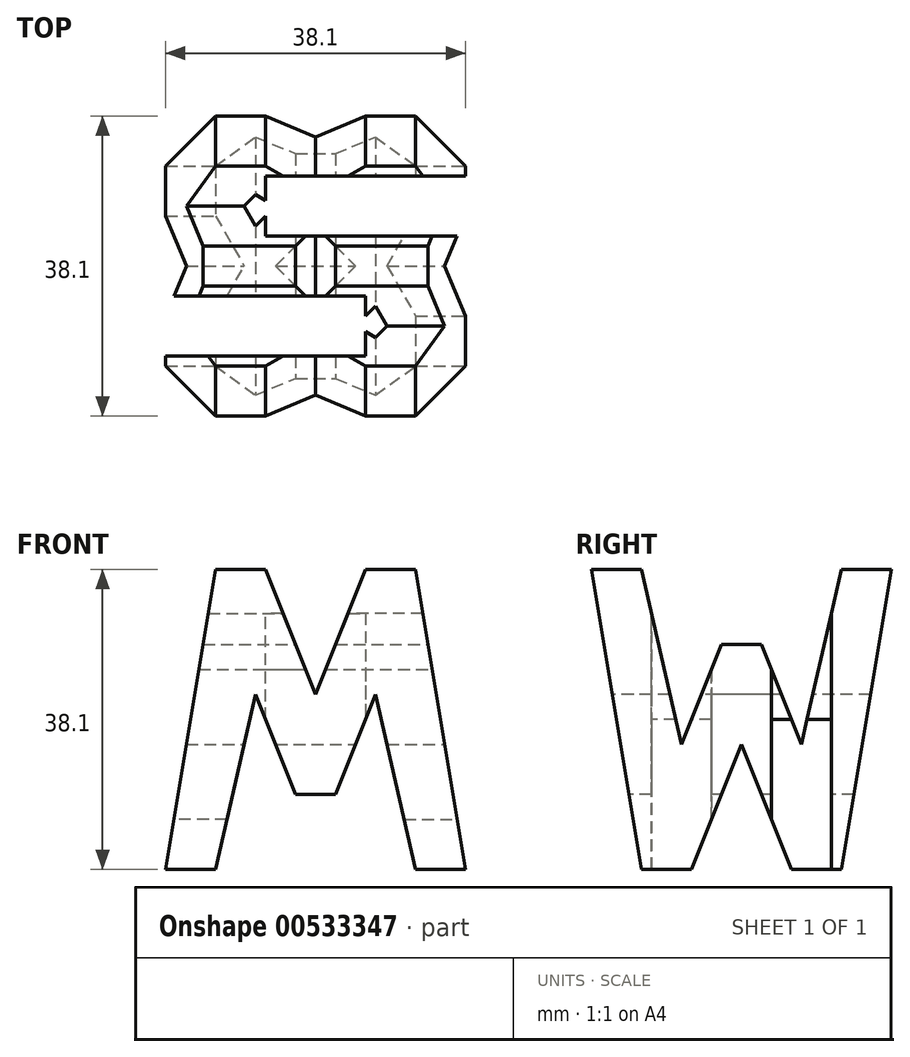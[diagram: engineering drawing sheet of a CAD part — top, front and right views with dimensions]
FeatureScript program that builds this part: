
annotation { "Feature Type Name" : "Feature", "Feature Type Description" : "" }
export const myFeature = defineFeature(function(context is Context, id is Id, definition is map)
    precondition{}
    {
        {
            var Q0;
            Q0=qCreatedBy(makeId("Front.planeOp"),FACE);
            var sketch = newSketch(context, id + "F0", { "sketchPlane" : qUnion([Q0])});
            skLineSegment(sketch, "E0", {"start": v(0, 0) * mm, "end": v(0, 38.1) * mm});
            skLineSegment(sketch, "E1", {"start": v(0, 38.1) * mm, "end": v(38.1, 38.1) * mm});
            skLineSegment(sketch, "E2", {"start": v(38.1, 38.1) * mm, "end": v(38.1, 0) * mm});
            skLineSegment(sketch, "E3", {"start": v(38.1, 0) * mm, "end": v(0, 0) * mm});
            skSolve(sketch);
        }
        {
            var Q0;
            Q0 = qSketchRegion(id + "F0", true);
            extrude(context, id + "F1", {"entities" : qUnion([Q0]), "depth" : 38.1 * mm, "offsetDistance" : 25.4 * mm});
        }
        {
            var Q0;
            Q0=qCreatedBy(makeId("Front.planeOp"),FACE);
            cPlane(context, id + "F2", {"entities" : qUnion([Q0]), "cplaneType" : CPlaneType.OFFSET, "offset" : 38.1 * mm, "width" : 152.4 * mm, "height" : 152.4 * mm});
        }
        {
            var Q0;
            Q0=qCreatedBy(makeId("Right.planeOp"),FACE);
            cPlane(context, id + "F3", {"entities" : qUnion([Q0]), "cplaneType" : CPlaneType.OFFSET, "offset" : 38.1 * mm, "width" : 152.4 * mm, "height" : 152.4 * mm});
        }
        {
            var Q0;
            Q0=qCreatedBy(makeId("Top.planeOp"),FACE);
            cPlane(context, id + "F4", {"entities" : qUnion([Q0]), "cplaneType" : CPlaneType.OFFSET, "offset" : 38.1 * mm, "width" : 152.4 * mm, "height" : 152.4 * mm});
        }
        {
            var Q0;
            Q0=qCreatedBy(id+"F3.planeOp",FACE);
            var sketch = newSketch(context, id + "F5", { "sketchPlane" : qUnion([Q0])});
            skLineSegment(sketch, "E4", {"start": v(-38.1, 38.1) * mm, "end": v(0, 38.1) * mm});
            skLineSegment(sketch, "E5", {"start": v(0, 38.1) * mm, "end": v(0, 0) * mm});
            skLineSegment(sketch, "E6", {"start": v(0, 0) * mm, "end": v(-38.1, 0) * mm});
            skLineSegment(sketch, "E7", {"start": v(-38.1, 0) * mm, "end": v(-38.1, 38.1) * mm});
            skLineSegment(sketch, "E8", {"start": v(-38.1, 38.1) * mm, "end": v(-31.75, 0) * mm});
            skLineSegment(sketch, "E9", {"start": v(0, 38.1) * mm, "end": v(-6.35, 0) * mm});
            skPoint(sketch, "E10.start.orphan", {"position": v(-28.95, 16.47) * mm});
            skPoint(sketch, "E11.end.orphan", {"position": v(-13.57, 16.47) * mm});
            skLineSegment(sketch, "E12", {"start": v(-6.35, 38.1) * mm, "end": v(-11.43, 15.87) * mm});
            skLineSegment(sketch, "E13", {"start": v(-26.67, 15.87) * mm, "end": v(-31.75, 38.1) * mm});
            skLineSegment(sketch, "E14", {"start": v(-19.05, 15.87) * mm, "end": v(-12.7, 0) * mm});
            skLineSegment(sketch, "E15", {"start": v(-19.05, 15.87) * mm, "end": v(-25.4, 0) * mm});
            skLineSegment(sketch, "E16", {"start": v(-26.67, 15.87) * mm, "end": v(-21.59, 28.57) * mm});
            skPoint(sketch, "E17.start.orphan", {"position": v(-21.6, 21.09) * mm});
            skPoint(sketch, "E18.end.orphan", {"position": v(-16.9, 28.57) * mm});
            skLineSegment(sketch, "E19", {"start": v(-21.6, 28.57) * mm, "end": v(-16.51, 28.57) * mm});
            skLineSegment(sketch, "E20", {"start": v(-16.51, 28.57) * mm, "end": v(-11.43, 15.87) * mm});
            skSolve(sketch);
        }
        {
            var Q0;
            {var subQ1=sQuery(id+"F5.wireOp",EDGE,"E12");Q0=makeQuery(id+"F5.imprint","IMPRINT",FACE,{"disambiguationData":[TD([[makeQuery(id+"F5.imprint","IMPRINT",EDGE,{"derivedFrom":subQ1}),-1.0]])]});}
            var Q1;
            {var subQ0=sQuery(id+"F5.wireOp",EDGE,"E7");Q1=makeQuery(id+"F5.imprint","IMPRINT",FACE,{"disambiguationData":[TD([[makeQuery(id+"F5.imprint","IMPRINT",EDGE,{"derivedFrom":subQ0}),-1.0]])]});}
            var Q2;
            {var subQ0=sQuery(id+"F5.wireOp",EDGE,"E14");Q2=makeQuery(id+"F5.imprint","IMPRINT",FACE,{"disambiguationData":[TD([[makeQuery(id+"F5.imprint","IMPRINT",EDGE,{"derivedFrom":subQ0}),-1.0]])]});}
            var Q3;
            {var subQ0=sQuery(id+"F5.wireOp",EDGE,"E5");Q3=makeQuery(id+"F5.imprint","IMPRINT",FACE,{"disambiguationData":[TD([[makeQuery(id+"F5.imprint","IMPRINT",EDGE,{"derivedFrom":subQ0}),-1.0]])]});}
            extrude(context, id + "F6", {"entities" : qUnion([Q0, Q1, Q2, Q3]), "operationType" : NewBodyOperationType.REMOVE, "oppositeDirection" : true, "depth" : 38.1 * mm, "offsetDistance" : 25.4 * mm});
        }
        {
            var Q0;
            Q0=qCreatedBy(id+"F2.planeOp",FACE);
            var sketch = newSketch(context, id + "F7", { "sketchPlane" : qUnion([Q0])});
            skLineSegment(sketch, "E21", {"start": v(0, 38.1) * mm, "end": v(38.1, 38.1) * mm});
            skLineSegment(sketch, "E22", {"start": v(38.1, 38.1) * mm, "end": v(38.1, 0) * mm});
            skLineSegment(sketch, "E23", {"start": v(38.1, 0) * mm, "end": v(0, 0) * mm});
            skLineSegment(sketch, "E24", {"start": v(0, 0) * mm, "end": v(0, 38.1) * mm});
            skLineSegment(sketch, "E25", {"start": v(6.35, 38.1) * mm, "end": v(0, 0) * mm});
            skLineSegment(sketch, "E26", {"start": v(12.7, 38.1) * mm, "end": v(19.05, 22.22) * mm});
            skLineSegment(sketch, "E27", {"start": v(19.05, 22.22) * mm, "end": v(25.4, 38.1) * mm});
            skLineSegment(sketch, "E28", {"start": v(31.75, 38.1) * mm, "end": v(38.1, 0) * mm});
            skLineSegment(sketch, "E29", {"start": v(16.51, 9.52) * mm, "end": v(21.6, 9.52) * mm});
            skLineSegment(sketch, "E30", {"start": v(21.6, 9.52) * mm, "end": v(26.67, 22.23) * mm});
            skLineSegment(sketch, "E31", {"start": v(26.67, 22.23) * mm, "end": v(31.75, 0) * mm});
            skPoint(sketch, "E32.start.orphan", {"position": v(11.43, 22.23) * mm});
            skLineSegment(sketch, "E33", {"start": v(6.35, 0) * mm, "end": v(11.43, 22.23) * mm});
            skLineSegment(sketch, "E34", {"start": v(11.43, 22.23) * mm, "end": v(16.51, 9.52) * mm});
            skSolve(sketch);
        }
        {
            var Q0;
            {var subQ0=sQuery(id+"F7.wireOp",EDGE,"E24");Q0=makeQuery(id+"F7.imprint","IMPRINT",FACE,{"disambiguationData":[TD([[makeQuery(id+"F7.imprint","IMPRINT",EDGE,{"derivedFrom":subQ0}),-1.0]])]});}
            var Q1;
            {var subQ0=sQuery(id+"F7.wireOp",EDGE,"E26");Q1=makeQuery(id+"F7.imprint","IMPRINT",FACE,{"disambiguationData":[TD([[makeQuery(id+"F7.imprint","IMPRINT",EDGE,{"derivedFrom":subQ0}),1.0]])]});}
            var Q2;
            {var subQ0=sQuery(id+"F7.wireOp",EDGE,"E22");Q2=makeQuery(id+"F7.imprint","IMPRINT",FACE,{"disambiguationData":[TD([[makeQuery(id+"F7.imprint","IMPRINT",EDGE,{"derivedFrom":subQ0}),-1.0]])]});}
            var Q3;
            Q3=makeQuery(id+"F7.imprint","IMPRINT",FACE,{"disambiguationData":[TD([[makeQuery(id+"F7.imprint","IMPRINT",EDGE,{"derivedFrom":sQuery(id+"F7.wireOp",EDGE,"E29")}),-1.0]])]});
            extrude(context, id + "F8", {"entities" : qUnion([Q0, Q1, Q2, Q3]), "operationType" : NewBodyOperationType.REMOVE, "oppositeDirection" : true, "depth" : 38.1 * mm, "offsetDistance" : 25.4 * mm});
        }
        {
            var Q0;
            Q0=qCreatedBy(id+"F4.planeOp",FACE);
            var sketch = newSketch(context, id + "F9", { "sketchPlane" : qUnion([Q0])});
            skLineSegment(sketch, "E35", {"start": v(0, 0) * mm, "end": v(38.1, 0) * mm});
            skLineSegment(sketch, "E36", {"start": v(38.1, 0) * mm, "end": v(38.1, -38.1) * mm});
            skLineSegment(sketch, "E37", {"start": v(38.1, -38.1) * mm, "end": v(0, -38.1) * mm});
            skLineSegment(sketch, "E38", {"start": v(0, -38.1) * mm, "end": v(0, 0) * mm});
            skLineSegment(sketch, "E39", {"start": v(38.1, -7.62) * mm, "end": v(12.7, -7.62) * mm});
            skLineSegment(sketch, "E40", {"start": v(38.1, -15.24) * mm, "end": v(12.7, -15.24) * mm});
            skLineSegment(sketch, "E41", {"start": v(12.7, -15.24) * mm, "end": v(12.7, -7.62) * mm});
            skLineSegment(sketch, "E42", {"start": v(0, -30.48) * mm, "end": v(25.4, -30.48) * mm});
            skLineSegment(sketch, "E43", {"start": v(25.4, -30.48) * mm, "end": v(25.4, -22.86) * mm});
            skLineSegment(sketch, "E44", {"start": v(25.4, -22.86) * mm, "end": v(0, -22.86) * mm});
            skSolve(sketch);
        }
        {
            var Q0;
            {var subQ0=sQuery(id+"F9.wireOp",EDGE,"E39");Q0=makeQuery(id+"F9.imprint","IMPRINT",FACE,{"disambiguationData":[TD([[makeQuery(id+"F9.imprint","IMPRINT",EDGE,{"derivedFrom":subQ0}),1.0]])]});}
            var Q1;
            {var subQ0=sQuery(id+"F9.wireOp",EDGE,"E42");Q1=makeQuery(id+"F9.imprint","IMPRINT",FACE,{"disambiguationData":[TD([[makeQuery(id+"F9.imprint","IMPRINT",EDGE,{"derivedFrom":subQ0}),1.0]])]});}
            extrude(context, id + "F10", {"entities" : qUnion([Q0, Q1]), "operationType" : NewBodyOperationType.REMOVE, "oppositeDirection" : true, "depth" : 38.1 * mm, "offsetDistance" : 25.4 * mm});
        }
    });
